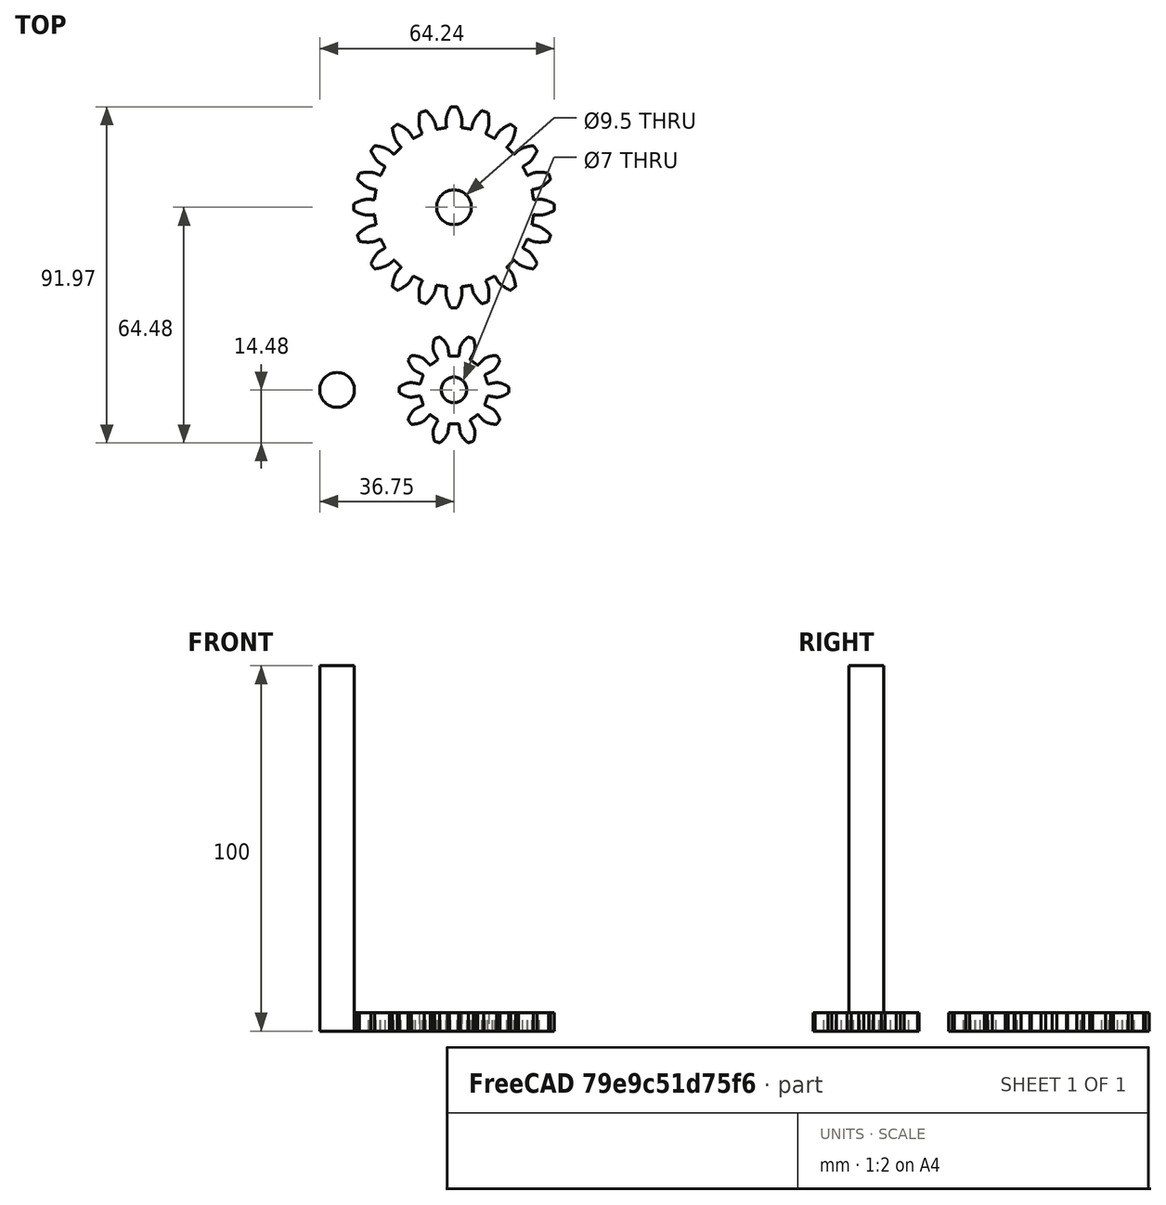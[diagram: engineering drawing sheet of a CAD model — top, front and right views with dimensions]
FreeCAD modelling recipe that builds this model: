
FCSTD DOCUMENT  (FreeCAD 0.17R13509 (Git))
Label: Gear_engranaje2ruedas
License: CreativeCommons Attribution-ShareAlike
LicenseURL: http://creativecommons.org/licenses/by-sa/4.0/
objects: Part::Cylinder×3, Part::FeaturePython×2, Part::Cut×2
note: 7 computed .brp shape members not serialized (recipe doc carries the construction recipe); baked Part::Feature solids carry a one-line shape summary decoded from their .brp

FEATURE [Part::FeaturePython] InvoluteGear  # WARN: FeaturePython — macro-defined, semantics opaque (R4)
  backlash = 0
  beta = 0
  clearance = 0.25
  double_helix = false
  head = 0
  height = 5
  module = 2.5
  numpoints = 6
  pressure_angle = 20
  reversed_backlash = false
  shift = 0
  simple = false
  teeth = 10
  undercut = false
FEATURE [Part::Cylinder] Cylinder  label="Cilindro"
  Angle = 360
  AttacherType = Attacher::AttachEngine3D
  Height = 10
  Placement = pos=(0,0,-3) rot=(0,0,1;0rad)
  Radius = 3.5
FEATURE [Part::Cut] Cut  label="Gear_small"
  Base = -> InvoluteGear
  Refine = true
  Tool = -> Cylinder
FEATURE [Part::FeaturePython] InvoluteGear001  # WARN: FeaturePython — macro-defined, semantics opaque (R4)
  Placement = pos=(0,50,0) rot=(0,0,1;0rad)
  backlash = 0
  beta = 0
  clearance = 0.25
  double_helix = false
  head = 0
  height = 5
  module = 2.5
  numpoints = 6
  pressure_angle = 20
  reversed_backlash = false
  shift = 0
  simple = false
  teeth = 20
  undercut = false
FEATURE [Part::Cylinder] Cylinder001  label="Cilindro001"
  Angle = 360
  AttacherType = Attacher::AttachEngine3D
  Height = 10
  Placement = pos=(0,50,-3) rot=(0,0,1;0rad)
  Radius = 4.75
FEATURE [Part::Cut] Cut001  label="Gear_big"
  Base = -> InvoluteGear001
  Refine = true
  Tool = -> Cylinder001
FEATURE [Part::Cylinder] Cylinder002  label="Eje"
  Angle = 360
  AttacherType = Attacher::AttachEngine3D
  Height = 100
  Placement = pos=(-32,0,0) rot=(0,0,1;0rad)
  Radius = 4.75
